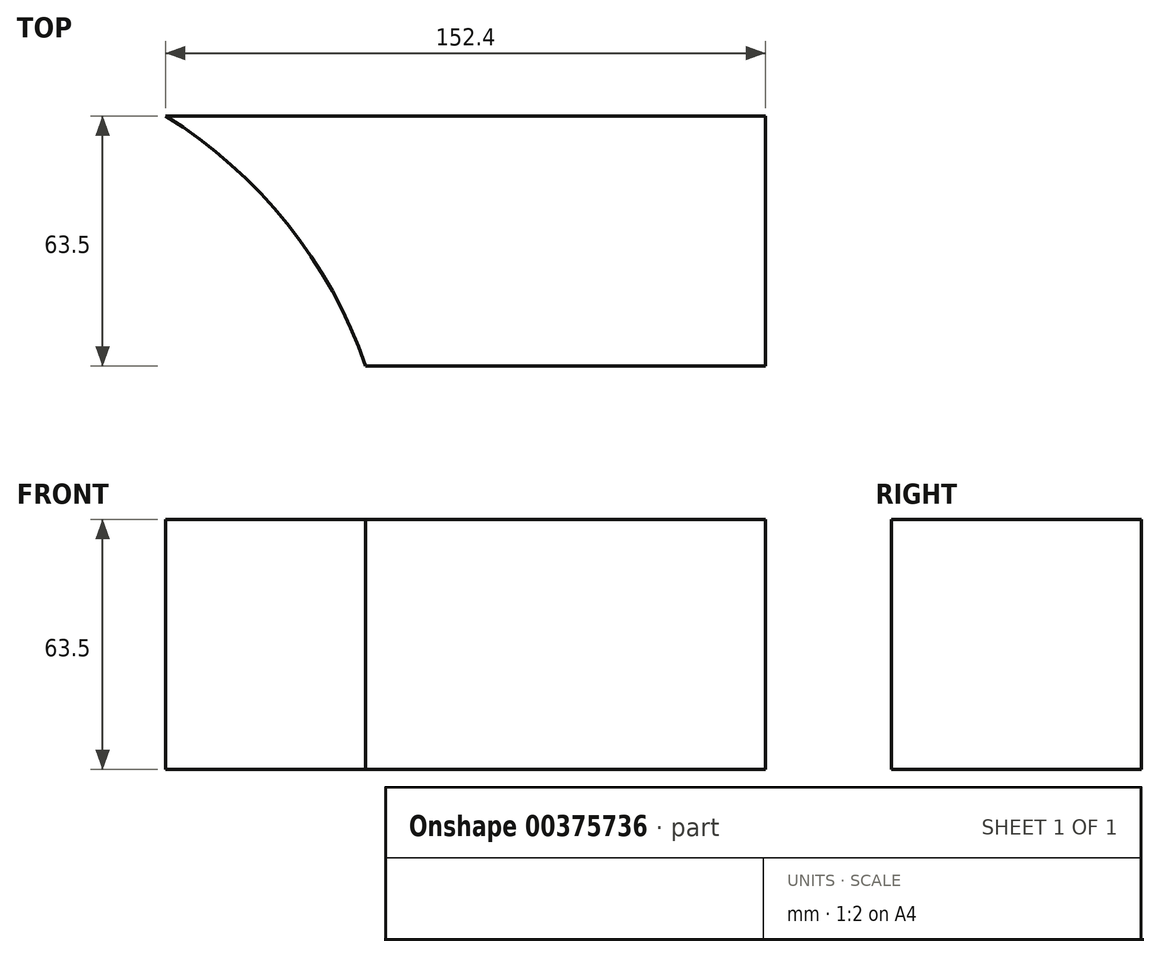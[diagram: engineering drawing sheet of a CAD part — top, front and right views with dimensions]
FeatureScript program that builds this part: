
annotation { "Feature Type Name" : "Feature", "Feature Type Description" : "" }
export const myFeature = defineFeature(function(context is Context, id is Id, definition is map)
    precondition{}
    {
        {
            var Q0;
            Q0=qCreatedBy(makeId("Front.planeOp"),FACE);
            var sketch = newSketch(context, id + "F0", { "sketchPlane" : qUnion([Q0])});
            skLineSegment(sketch, "E0.bottom", {"start": v(0, 0) * mm, "end": v(152.4, 0) * mm});
            skLineSegment(sketch, "E0.top", {"start": v(0, 63.5) * mm, "end": v(152.4, 63.5) * mm});
            skLineSegment(sketch, "E0.left", {"start": v(0, 0) * mm, "end": v(0, 63.5) * mm});
            skLineSegment(sketch, "E0.right", {"start": v(152.4, 0) * mm, "end": v(152.4, 63.5) * mm});
            skSolve(sketch);
        }
        {
            var Q0;
            Q0=makeQuery(id+"F0.imprint","IMPRINT",FACE,{"disambiguationData":[TD([[makeQuery(id+"F0.imprint","IMPRINT",EDGE,{"derivedFrom":sQuery(id+"F0.wireOp",EDGE,"E0.bottom")}),1.0]])]});
            extrude(context, id + "F1", {"entities" : qUnion([Q0]), "depth" : 63.5 * mm});
        }
        {
            var Q0;
            Q0=makeQuery(id+"F1.opExtrude","SWEPT_FACE",FACE,{"disambiguationData":[OSD([sQuery(id+"F0.wireOp",EDGE,"E0.bottom")])]});
            var sketch = newSketch(context, id + "F2", { "sketchPlane" : qUnion([Q0])});
            skArc(sketch, "E1", {"start": v(0, 0) * mm, "mid": v(30.9, 27.35) * mm, "end": v(50.8, 63.5) * mm});
            skSolve(sketch);
        }
        {
            var Q0;
            {var subQ0=sQuery(id+"F2.wireOp",EDGE,"E1");Q0=makeQuery(id+"F2.imprint","IMPRINT",FACE,{"disambiguationData":[TD([[makeQuery(id+"F2.imprint","IMPRINT",EDGE,{"derivedFrom":subQ0}),1.0]])]});}
            extrude(context, id + "F3", {"entities" : qUnion([Q0]), "operationType" : NewBodyOperationType.REMOVE, "endBound" : BoundingType.THROUGH_ALL, "oppositeDirection" : true, "depth" : 25.4 * mm});
        }
    });
